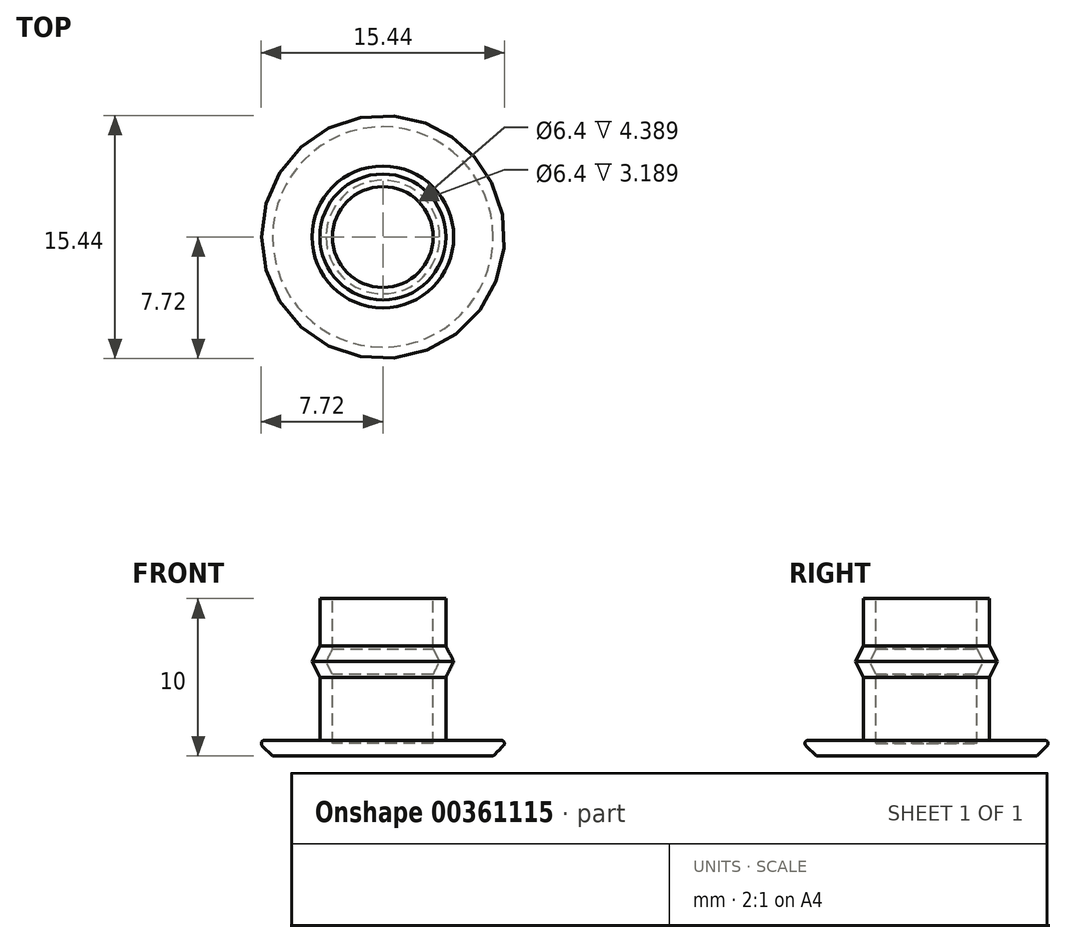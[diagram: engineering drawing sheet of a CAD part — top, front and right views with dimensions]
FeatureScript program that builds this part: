
annotation { "Feature Type Name" : "Feature", "Feature Type Description" : "" }
export const myFeature = defineFeature(function(context is Context, id is Id, definition is map)
    precondition{}
    {
        {
            var Q0;
            Q0=qCreatedBy(makeId("Front.planeOp"),FACE);
            var sketch = newSketch(context, id + "F0", { "sketchPlane" : qUnion([Q0])});
            skLineSegment(sketch, "E0", {"start": v(0, 0) * mm, "end": v(8, 0) * mm});
            skLineSegment(sketch, "E1", {"start": v(8, 0) * mm, "end": v(8, 1) * mm});
            skLineSegment(sketch, "E2", {"start": v(8, 1) * mm, "end": v(4, 1) * mm});
            skLineSegment(sketch, "E3", {"start": v(4, 1) * mm, "end": v(4, 5) * mm});
            skLineSegment(sketch, "E4", {"start": v(4, 10) * mm, "end": v(0, 10) * mm});
            skLineSegment(sketch, "E5", {"start": v(0, 10) * mm, "end": v(0, 0) * mm});
            skLineSegment(sketch, "E6", {"start": v(4, 7) * mm, "end": v(4.5, 6) * mm});
            skLineSegment(sketch, "E7", {"start": v(4.5, 6) * mm, "end": v(4, 5) * mm});
            skLineSegment(sketch, "E8.trimOffspring", {"start": v(4, 7) * mm, "end": v(4, 10) * mm});
            skSolve(sketch);
        }
        {
            var Q0;
            Q0 = qSketchRegion(id + "F0", true);
            var Q1;
            Q1=sQuery(id+"F0.wireOp",EDGE,"E5");
            revolve(context, id + "F1", {"entities" : qUnion([Q0]), "axis" : qUnion([Q1]), "revolveType" : RevolveType.FULL});
        }
        {
            var Q0;
            Q0=makeQuery(id+"F1.opRevolve","SWEPT_FACE",FACE,{"disambiguationData":[OSD([sQuery(id+"F0.wireOp",EDGE,"E4")])]});
            shell(context, id + "F2", {"entities" : qUnion([Q0]), "thickness" : 0.8 * mm});
        }
        {
            var Q0;
            Q0=makeQuery(id+"F1.opRevolve","SWEPT_EDGE",EDGE,{"disambiguationData":[OSD([sQuery(id+"F0.wireOp",EDGE,"E0"),sQuery(id+"F0.wireOp",EDGE,"E1")])]});
            chamfer(context, id + "F3", {"entities" : qUnion([Q0]), "width" : 1 * mm, "tangentPropagation" : true});
        }
        {
            var Q0;
            Q0=makeQuery(id+"F3.opChamfer","BLEND_EDGE",EDGE,{"blendedFrom":[makeQuery(id+"F1.opRevolve","SWEPT_EDGE",EDGE,{"disambiguationData":[OSD([sQuery(id+"F0.wireOp",EDGE,"E0"),sQuery(id+"F0.wireOp",EDGE,"E1")])]}),makeQuery(id+"F1.opRevolve","SWEPT_FACE",FACE,{"disambiguationData":[OSD([sQuery(id+"F0.wireOp",EDGE,"E2")])]})],"blendedInto":[makeQuery(id+"F1.opRevolve","SWEPT_FACE",FACE,{"disambiguationData":[OSD([sQuery(id+"F0.wireOp",EDGE,"E2")])]})]});
            fillet(context, id + "F4", {"entities" : qUnion([Q0]), "radius" : 0.2 * mm, "tangentPropagation" : true, "allowEdgeOverflow" : false});
        }
    });
